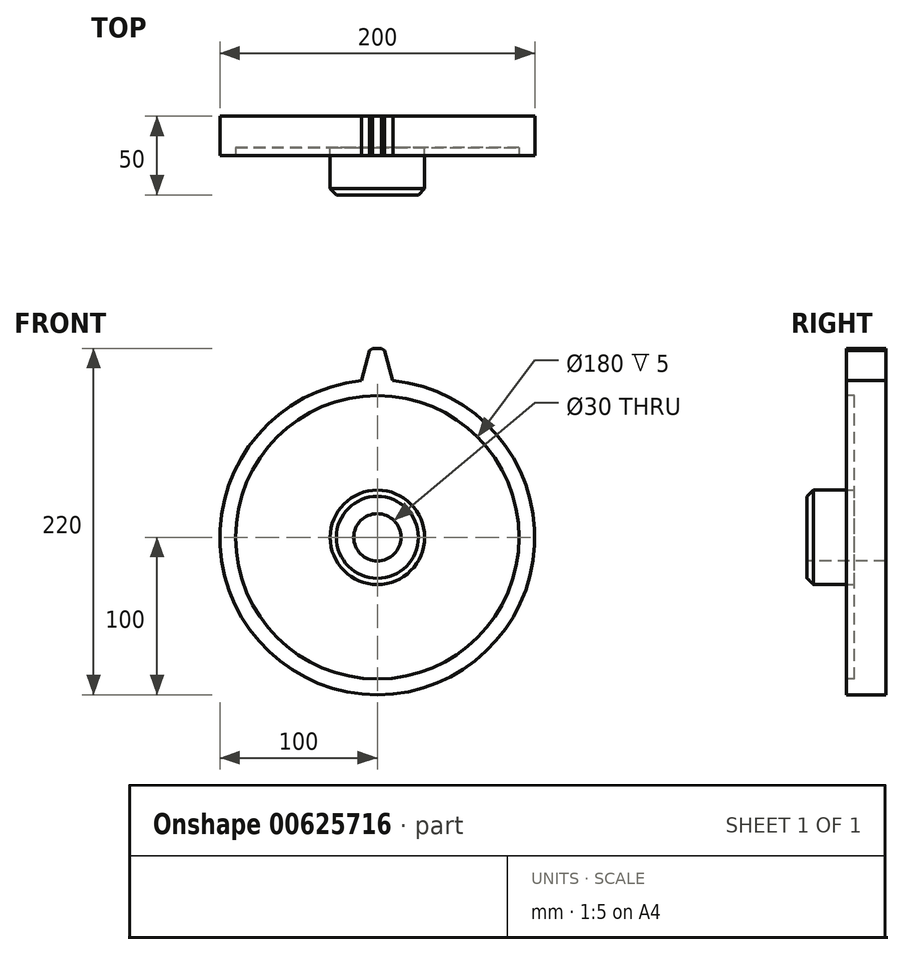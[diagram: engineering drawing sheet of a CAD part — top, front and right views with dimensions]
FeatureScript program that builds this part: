
annotation { "Feature Type Name" : "Feature", "Feature Type Description" : "" }
export const myFeature = defineFeature(function(context is Context, id is Id, definition is map)
    precondition{}
    {
        {
            var Q0;
            Q0=qCreatedBy(makeId("Front.planeOp"),FACE);
            var sketch = newSketch(context, id + "F0", { "sketchPlane" : qUnion([Q0])});
            skCircle(sketch, "E0", {"center": v(0, 0) * mm, "radius": 100 * mm});
            skSolve(sketch);
        }
        {
            var Q0;
            Q0=qCreatedBy(makeId("Front.planeOp"),FACE);
            var sketch = newSketch(context, id + "F1", { "sketchPlane" : qUnion([Q0])});
            skLineSegment(sketch, "E1", {"start": v(9.81, 99.52) * mm, "end": v(-10.17, 99.48) * mm});
            skLineSegment(sketch, "E2", {"start": v(-10.17, 99.48) * mm, "end": v(-4.72, 120) * mm});
            skLineSegment(sketch, "E3", {"start": v(-4.72, 120) * mm, "end": v(4.28, 120) * mm});
            skLineSegment(sketch, "E4", {"start": v(4.28, 120) * mm, "end": v(9.81, 99.52) * mm});
            skSolve(sketch);
        }
        {
            var Q0;
            Q0 = qSketchRegion(id + "F0", true);
            extrude(context, id + "F2", {"entities" : qUnion([Q0]), "depth" : 25 * mm, "offsetDistance" : 25 * mm});
        }
        {
            var Q0;
            Q0=makeQuery(id+"F1.imprint","IMPRINT",FACE,{"disambiguationData":[TD([[makeQuery(id+"F1.imprint","IMPRINT",EDGE,{"derivedFrom":sQuery(id+"F1.wireOp",EDGE,"E1")}),-1.0]])]});
            var Q1;
            Q1=makeQuery(id+"F2.opExtrude","CAP_FACE",FACE,{"disambiguationData":[OSD([sQuery(id+"F0.wireOp",EDGE,"E0")])],"isStart":false});
            extrude(context, id + "F3", {"entities" : qUnion([Q0]), "operationType" : NewBodyOperationType.ADD, "endBound" : BoundingType.UP_TO_SURFACE, "depth" : 25 * mm, "endBoundEntityFace" : qUnion([Q1]), "offsetDistance" : 25 * mm});
        }
        {
            var Q0;
            Q0=makeQuery(id+"F3.opExtrude","SWEPT_EDGE",EDGE,{"disambiguationData":[OSD([sQuery(id+"F1.wireOp",EDGE,"E1"),sQuery(id+"F1.wireOp",EDGE,"E2")])]});
            var Q1;
            Q1=makeQuery(id+"F3.opExtrude","SWEPT_EDGE",EDGE,{"disambiguationData":[OSD([sQuery(id+"F1.wireOp",EDGE,"E1"),sQuery(id+"F1.wireOp",EDGE,"E4")])]});
            fillet(context, id + "F4", {"entities" : qUnion([Q0, Q1]), "radius" : 5 * mm, "tangentPropagation" : true, "allowEdgeOverflow" : false});
        }
        {
            var Q0;
            Q0=makeQuery(id+"F3.opExtrude","SWEPT_EDGE",EDGE,{"disambiguationData":[OSD([sQuery(id+"F1.wireOp",EDGE,"E2"),sQuery(id+"F1.wireOp",EDGE,"E3")])]});
            var Q1;
            Q1=makeQuery(id+"F3.opExtrude","SWEPT_EDGE",EDGE,{"disambiguationData":[OSD([sQuery(id+"F1.wireOp",EDGE,"E3"),sQuery(id+"F1.wireOp",EDGE,"E4")])]});
            chamfer(context, id + "F5", {"entities" : qUnion([Q0, Q1]), "width" : 2 * mm, "tangentPropagation" : true});
        }
        {
            var Q0;
            {var subQ0=sQuery(id+"F0.wireOp",EDGE,"E0");Q0=makeQuery(id+"FKvSvNCsyhTZhGM_1.19.F3.boolean.opBoolean","MERGE",FACE,{"derivedFrom":[makeQuery(id+"FKvSvNCsyhTZhGM_1.18.F3.boolean.opBoolean","MERGE",FACE,{"derivedFrom":[makeQuery(id+"FKvSvNCsyhTZhGM_1.17.F3.boolean.opBoolean","MERGE",FACE,{"derivedFrom":[makeQuery(id+"FKvSvNCsyhTZhGM_1.16.F3.boolean.opBoolean","MERGE",FACE,{"derivedFrom":[makeQuery(id+"FKvSvNCsyhTZhGM_1.15.F3.boolean.opBoolean","MERGE",FACE,{"derivedFrom":[makeQuery(id+"FKvSvNCsyhTZhGM_1.14.F3.boolean.opBoolean","MERGE",FACE,{"derivedFrom":[makeQuery(id+"FKvSvNCsyhTZhGM_1.13.F3.boolean.opBoolean","MERGE",FACE,{"derivedFrom":[makeQuery(id+"FKvSvNCsyhTZhGM_1.12.F3.boolean.opBoolean","MERGE",FACE,{"derivedFrom":[makeQuery(id+"FKvSvNCsyhTZhGM_1.11.F3.boolean.opBoolean","MERGE",FACE,{"derivedFrom":[makeQuery(id+"FKvSvNCsyhTZhGM_1.10.F3.boolean.opBoolean","MERGE",FACE,{"derivedFrom":[makeQuery(id+"FKvSvNCsyhTZhGM_1.9.F3.boolean.opBoolean","MERGE",FACE,{"derivedFrom":[makeQuery(id+"FKvSvNCsyhTZhGM_1.8.F3.boolean.opBoolean","MERGE",FACE,{"derivedFrom":[makeQuery(id+"FKvSvNCsyhTZhGM_1.7.F3.boolean.opBoolean","MERGE",FACE,{"derivedFrom":[makeQuery(id+"FKvSvNCsyhTZhGM_1.6.F3.boolean.opBoolean","MERGE",FACE,{"derivedFrom":[makeQuery(id+"FKvSvNCsyhTZhGM_1.5.F3.boolean.opBoolean","MERGE",FACE,{"derivedFrom":[makeQuery(id+"FKvSvNCsyhTZhGM_1.4.F3.boolean.opBoolean","MERGE",FACE,{"derivedFrom":[makeQuery(id+"FKvSvNCsyhTZhGM_1.3.F3.boolean.opBoolean","MERGE",FACE,{"derivedFrom":[makeQuery(id+"FKvSvNCsyhTZhGM_1.2.F3.boolean.opBoolean","MERGE",FACE,{"derivedFrom":[makeQuery(id+"FKvSvNCsyhTZhGM_1.1.F3.boolean.opBoolean","MERGE",FACE,{"derivedFrom":[makeQuery(id+"F3.boolean.opBoolean","MERGE",FACE,{"derivedFrom":[makeQuery(id+"F2.opExtrude","CAP_FACE",FACE,{"disambiguationData":[OSD([subQ0])],"isStart":false}),makeQuery(id+"F3.opExtrude","CAP_FACE",FACE,{"disambiguationData":[OSD([subQ0])],"isStart":false})]}),makeQuery(id+"FKvSvNCsyhTZhGM_1.1.F3.opExtrude","CAP_FACE",FACE,{"disambiguationData":[OSD([subQ0])],"isStart":false})]}),makeQuery(id+"FKvSvNCsyhTZhGM_1.2.F3.opExtrude","CAP_FACE",FACE,{"disambiguationData":[OSD([subQ0])],"isStart":false})]}),makeQuery(id+"FKvSvNCsyhTZhGM_1.3.F3.opExtrude","CAP_FACE",FACE,{"disambiguationData":[OSD([subQ0])],"isStart":false})]}),makeQuery(id+"FKvSvNCsyhTZhGM_1.4.F3.opExtrude","CAP_FACE",FACE,{"disambiguationData":[OSD([subQ0])],"isStart":false})]}),makeQuery(id+"FKvSvNCsyhTZhGM_1.5.F3.opExtrude","CAP_FACE",FACE,{"disambiguationData":[OSD([subQ0])],"isStart":false})]}),makeQuery(id+"FKvSvNCsyhTZhGM_1.6.F3.opExtrude","CAP_FACE",FACE,{"disambiguationData":[OSD([subQ0])],"isStart":false})]}),makeQuery(id+"FKvSvNCsyhTZhGM_1.7.F3.opExtrude","CAP_FACE",FACE,{"disambiguationData":[OSD([subQ0])],"isStart":false})]}),makeQuery(id+"FKvSvNCsyhTZhGM_1.8.F3.opExtrude","CAP_FACE",FACE,{"disambiguationData":[OSD([subQ0])],"isStart":false})]}),makeQuery(id+"FKvSvNCsyhTZhGM_1.9.F3.opExtrude","CAP_FACE",FACE,{"disambiguationData":[OSD([subQ0])],"isStart":false})]}),makeQuery(id+"FKvSvNCsyhTZhGM_1.10.F3.opExtrude","CAP_FACE",FACE,{"disambiguationData":[OSD([subQ0])],"isStart":false})]}),makeQuery(id+"FKvSvNCsyhTZhGM_1.11.F3.opExtrude","CAP_FACE",FACE,{"disambiguationData":[OSD([subQ0])],"isStart":false})]}),makeQuery(id+"FKvSvNCsyhTZhGM_1.12.F3.opExtrude","CAP_FACE",FACE,{"disambiguationData":[OSD([subQ0])],"isStart":false})]}),makeQuery(id+"FKvSvNCsyhTZhGM_1.13.F3.opExtrude","CAP_FACE",FACE,{"disambiguationData":[OSD([subQ0])],"isStart":false})]}),makeQuery(id+"FKvSvNCsyhTZhGM_1.14.F3.opExtrude","CAP_FACE",FACE,{"disambiguationData":[OSD([subQ0])],"isStart":false})]}),makeQuery(id+"FKvSvNCsyhTZhGM_1.15.F3.opExtrude","CAP_FACE",FACE,{"disambiguationData":[OSD([subQ0])],"isStart":false})]}),makeQuery(id+"FKvSvNCsyhTZhGM_1.16.F3.opExtrude","CAP_FACE",FACE,{"disambiguationData":[OSD([subQ0])],"isStart":false})]}),makeQuery(id+"FKvSvNCsyhTZhGM_1.17.F3.opExtrude","CAP_FACE",FACE,{"disambiguationData":[OSD([subQ0])],"isStart":false})]}),makeQuery(id+"FKvSvNCsyhTZhGM_1.18.F3.opExtrude","CAP_FACE",FACE,{"disambiguationData":[OSD([subQ0])],"isStart":false})]}),makeQuery(id+"FKvSvNCsyhTZhGM_1.19.F3.opExtrude","CAP_FACE",FACE,{"disambiguationData":[OSD([subQ0])],"isStart":false})]});}
            var sketch = newSketch(context, id + "F6", { "sketchPlane" : qUnion([Q0])});
            skCircle(sketch, "E5", {"center": v(0, 0) * mm, "radius": 90 * mm});
            skSolve(sketch);
        }
        {
            var Q0;
            Q0=makeQuery(id+"F6.imprint","IMPRINT",FACE,{"disambiguationData":[TD([[makeQuery(id+"F6.imprint","IMPRINT",EDGE,{"derivedFrom":sQuery(id+"F6.wireOp",EDGE,"E5")}),1.0]])]});
            extrude(context, id + "F7", {"entities" : qUnion([Q0]), "operationType" : NewBodyOperationType.REMOVE, "oppositeDirection" : true, "depth" : 5 * mm, "offsetDistance" : 25 * mm});
        }
        {
            var Q0;
            Q0=makeQuery(id+"F7.boolean.opBoolean","COPY",FACE,{"derivedFrom":makeQuery(id+"F7.opExtrude","CAP_FACE",FACE,{"disambiguationData":[OSD([sQuery(id+"F6.wireOp",EDGE,"E5")])],"isStart":false})});
            var sketch = newSketch(context, id + "F8", { "sketchPlane" : qUnion([Q0])});
            skCircle(sketch, "E6", {"center": v(0, 0) * mm, "radius": 30 * mm});
            skSolve(sketch);
        }
        {
            var Q0;
            Q0 = qSketchRegion(id + "F8", true);
            extrude(context, id + "F9", {"entities" : qUnion([Q0]), "operationType" : NewBodyOperationType.ADD, "depth" : 30 * mm, "offsetDistance" : 25 * mm});
        }
        {
            var Q0;
            Q0=makeQuery(id+"F9.opExtrude","CAP_FACE",FACE,{"disambiguationData":[OSD([sQuery(id+"F8.wireOp",EDGE,"E6")])],"isStart":false});
            var sketch = newSketch(context, id + "F10", { "sketchPlane" : qUnion([Q0])});
            skCircle(sketch, "E7", {"center": v(0, 0) * mm, "radius": 15 * mm});
            skSolve(sketch);
        }
        {
            var Q0;
            Q0 = qSketchRegion(id + "F10", true);
            extrude(context, id + "F11", {"entities" : qUnion([Q0]), "operationType" : NewBodyOperationType.REMOVE, "endBound" : BoundingType.THROUGH_ALL, "oppositeDirection" : true, "depth" : 25 * mm, "offsetDistance" : 25 * mm});
        }
        {
            var Q0;
            Q0=makeQuery(id+"F9.opExtrude","CAP_EDGE",EDGE,{"disambiguationData":[OSD([sQuery(id+"F8.wireOp",EDGE,"E6")])],"isStart":false});
            var Q1;
            Q1=makeQuery(id+"F11.boolean.opBoolean","COPY",EDGE,{"derivedFrom":makeQuery(id+"F11.opExtrude","CAP_EDGE",EDGE,{"disambiguationData":[OSD([sQuery(id+"F10.wireOp",EDGE,"E7")])],"isStart":true})});
            chamfer(context, id + "F12", {"entities" : qUnion([Q0, Q1]), "width" : 4 * mm, "tangentPropagation" : true});
        }
    });
